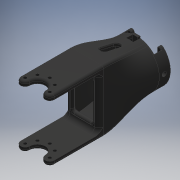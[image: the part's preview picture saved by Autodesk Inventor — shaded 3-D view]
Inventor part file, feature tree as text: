
AUTODESK INVENTOR PART (.ipt)
format: ipt  version: 2019 (Build 230136000, 136)  size: 949,248 bytes
history: native  units: mm
features: extrude x15, sketch x15, projected_geometry x9, fillet x5, plane x4, chamfer x3, loft x2, mirror x1, hole x1, pattern_circular x1, emboss x1
ambient origin geometry x8: Origin, YZ Plane, XZ Plane, XY Plane, X Axis, Y Axis, Z Axis, Center Point
bodies: Solid1 (feature_tree)
feature tree (57):
  extrude  "Extrusion1"  Depth=47.0mm
  extrude  "Extrusion2"  Depth=25.0mm
  plane  "Work Plane1"
  plane  "Work Plane2"
  extrude  "Extrusion3"  Depth=40.0mm
  mirror  "Mirror1"
  extrude  "Extrusion13"  Depth=2.8mm
  extrude  "Extrusion14"  Depth=7.0mm
  fillet  "Fillet10"  [1 undecoded]
  fillet  "Fillet3"  [1 undecoded]
  fillet  "Fillet12"  Radius=4.0mm
  sketch  "Sketch18"  dims[d47=2.0mm d97=30.25mm]
  plane  "Work Plane5"
  extrude  "Extrusion16"  Depth=2.0mm
  chamfer  "Chamfer3"  Distance=25.0mm
  sketch  "Sketch22"  dims[d102=4.0mm]
  extrude  "Extrusion20"  Depth=10.0mm TaperAngle=0.0deg
  extrude  "Extrusion21"  Depth=2.5mm
  chamfer  "Chamfer2"  Distance=2.0mm
  sketch  "Sketch24"  dims[d105=2.5mm]
  loft  "Loft2"
  loft  "Loft3"
  extrude  "Extrusion15"  Depth=1.75mm TaperAngle=0.0deg
  extrude  "Extrusion27"  Depth=1.75mm
  plane  "Work Plane6"
  hole  "Hole1"  [1 undecoded]
  pattern_circular  "Circular Pattern1"  [2 undecoded]
  fillet  "Fillet13"  Radius=1.0mm
  sketch  "Sketch26"  dims[d113=10.0mm d114=4.0mm d115=0.0mm]
  extrude  "Extrusion22"  Depth=2.0mm TaperAngle=45.0deg
  emboss  "Emboss1"
  fillet  "Fillet14"  Radius=5.0mm
  sketch  "Sketch27"  dims[d116=4.0mm d120=2.5mm]
  extrude  "Extrusion23"  Depth=1.75mm TaperAngle=0.0deg
  extrude  "Extrusion24"  Depth=1.75mm
  sketch  "Sketch28"  dims[d121=6.25mm]
  extrude  "Extrusion25"  Depth=1.75mm
  extrude  "Extrusion26"  Depth=1.75mm
  chamfer  "Chamfer4"  Distance=25.0mm
  sketch  "Sketch1"  dims[d0=30.0mm d1=47.0mm]
  sketch  "Sketch2"  dims[d2=4.0mm d3=0.0mm d4=25.0mm]
  sketch  "Sketch3"  dims[d6=40.0mm d7=0.0mm d8=40.0mm]
  projected_geometry  "Projected Loop1"
  sketch  "Sketch15"  dims[d9=22.0mm d10=2.8mm]
  sketch  "Sketch16"  dims[d11=80.0mm d13=360.0deg d15=7.0mm d16=180.0deg d17=180.0deg d18=4.0mm d19=0.0mm]
  projected_geometry  "Projected Loop12"
  projected_geometry  "Projected Loop14"
  sketch  "Sketch20"  dims[d99=52.5mm]
  sketch  "Sketch21"  dims[d101=4.0mm]
  projected_geometry  "Projected Loop15"
  projected_geometry  "Projected Loop18"
  sketch  "Sketch25"  dims[d106=2.5mm d111=25.0mm d112=0.0mm]
  projected_geometry  "Projected Loop19"
  projected_geometry  "Projected Loop20"
  projected_geometry  "Projected Loop21"
  sketch  "Sketch29"  dims[d123=4.0mm d129=2.0mm d132=10.0mm d133=90.0deg d136=10.0mm d137=90.0deg d138=21.0mm d139=4.0mm d140=0.0mm d141=11.25mm d142=4.0mm d143=0.0mm d144=6.0mm d145=1.0mm d146=0.5mm d147=2.0mm d148=45.0deg d150=5.0mm d151=2.0mm d152=45.0deg d163=15.0mm d164=0.0mm d165=42.0mm d166=80.0mm d167=19.125mm d168=25.0mm d169=10.0mm d170=0.0mm d171=10.0mm d172=0.0mm d173=2.5mm d174=10.0mm d175=90.0deg d176=10.0mm d177=90.0deg d178=-6.0mm d179=2.25mm d180=6.0mm d181=4.0mm d182=4.0mm d183=90.0deg d184=8.0mm d185=20.594885mm d186=40.0mm d187=360.0deg d189=2.0mm d190=12.0mm d191=6.0mm d192=2.0mm d193=10.0mm d194=0.0mm d195=1.0mm d196=0.0mm d197=1.0mm d198=0.75mm d199=25.0mm d201=5.0mm d202=20.0mm d204=0.75mm d205=7.0mm d206=0.0mm d207=2.0mm d208=0.0mm d209=40.0mm d210=3.0mm d211=0.0mm d212=1.0mm d213=25.307274mm d214=30.25mm d215=30.543262mm d216=5.0mm d217=5.0mm d218=2.0mm d219=0.0mm d220=5.0mm d221=0.0mm d222=0.5mm d223=0.5mm d224=0.5mm d225=2.0mm d226=45.0deg d227=5.0mm d228=2.0mm d229=5.0mm d230=0.0mm d231=1.75mm]
  projected_geometry  "Projected Loop22"
note: 5 required parameter values undecoded (feature->parameter linkage not recoverable at this tier; creation-order binding heuristic only, values carry confidence <= 0.55)
